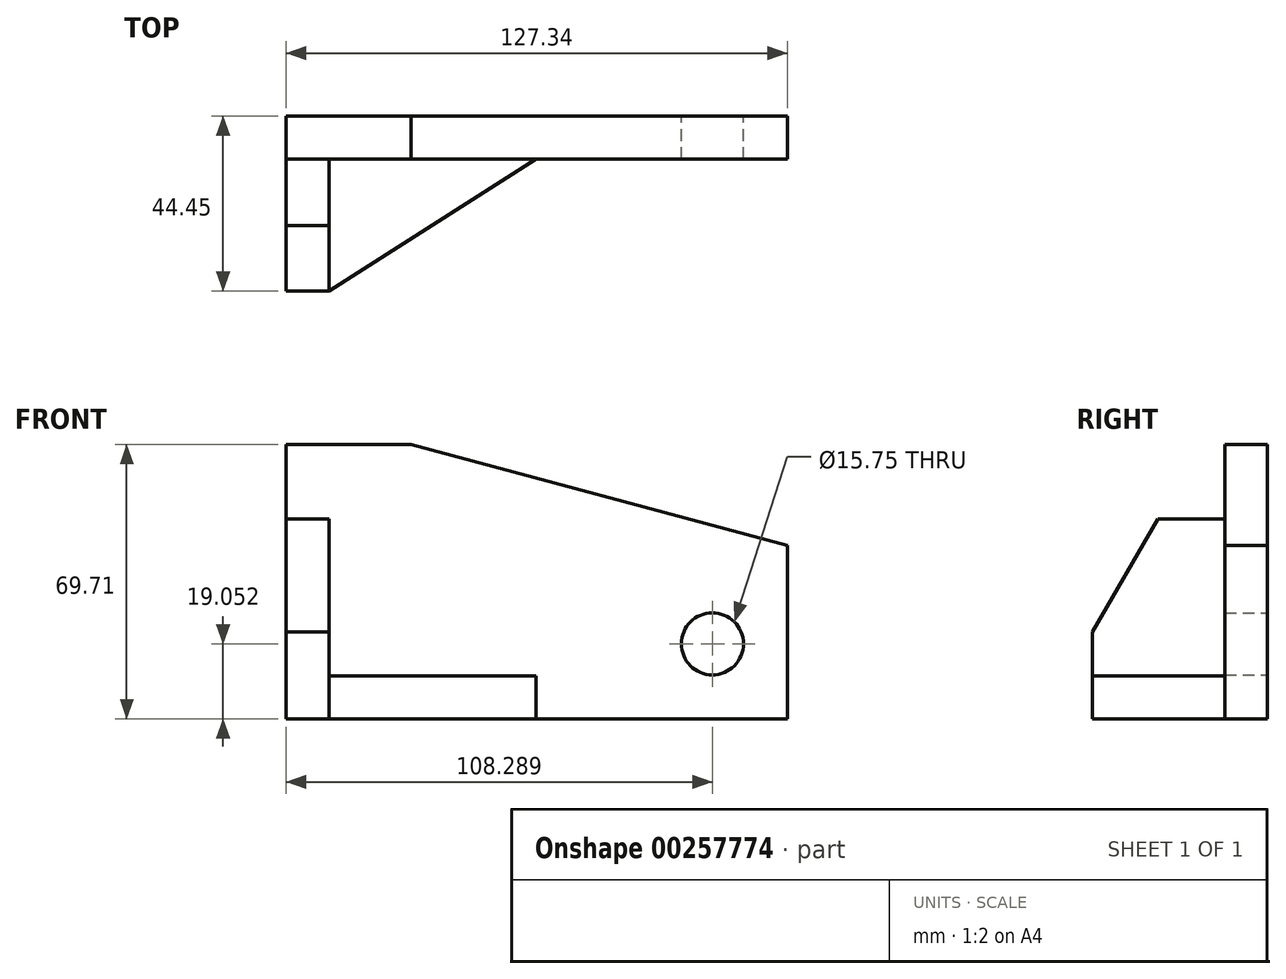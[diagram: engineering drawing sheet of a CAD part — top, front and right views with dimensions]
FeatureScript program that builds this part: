
annotation { "Feature Type Name" : "Feature", "Feature Type Description" : "" }
export const myFeature = defineFeature(function(context is Context, id is Id, definition is map)
    precondition{}
    {
        {
            var Q0;
            Q0=qCreatedBy(makeId("Front.planeOp"),FACE);
            var sketch = newSketch(context, id + "F0", { "sketchPlane" : qUnion([Q0])});
            skLineSegment(sketch, "E0.bottom", {"start": v(-78.15, 58.66) * mm, "end": v(-46.4, 58.66) * mm});
            skLineSegment(sketch, "E0.top", {"start": v(-78.15, -11.05) * mm, "end": v(49.19, -11.05) * mm});
            skLineSegment(sketch, "E0.left", {"start": v(-78.15, 58.66) * mm, "end": v(-78.15, -11.05) * mm});
            skLineSegment(sketch, "E0.right", {"start": v(49.19, 33.04) * mm, "end": v(49.19, -11.05) * mm});
            skLineSegment(sketch, "E1", {"start": v(-46.4, 58.66) * mm, "end": v(49.19, 33.04) * mm});
            skCircle(sketch, "E2", {"center": v(30.14, 8) * mm, "radius": 7.87 * mm});
            skSolve(sketch);
        }
        {
            var Q0;
            Q0=makeQuery(id+"F0.imprint","IMPRINT",FACE,{"disambiguationData":[TD([[makeQuery(id+"F0.imprint","IMPRINT",EDGE,{"derivedFrom":sQuery(id+"F0.wireOp",EDGE,"E0.bottom")}),-1.0]])]});
            extrude(context, id + "F1", {"entities" : qUnion([Q0]), "depth" : 10.92 * mm});
        }
        {
            var Q0;
            Q0=makeQuery(id+"F1.opExtrude","CAP_FACE",FACE,{"disambiguationData":[OSD([sQuery(id+"F0.wireOp",EDGE,"E0.bottom"),sQuery(id+"F0.wireOp",EDGE,"E0.top"),sQuery(id+"F0.wireOp",EDGE,"E0.left"),sQuery(id+"F0.wireOp",EDGE,"E0.right"),sQuery(id+"F0.wireOp",EDGE,"E1")])],"isStart":false});
            var sketch = newSketch(context, id + "F2", { "sketchPlane" : qUnion([Q0])});
            skLineSegment(sketch, "E3.bottom", {"start": v(-78.15, 39.75) * mm, "end": v(-67.22, 39.75) * mm});
            skLineSegment(sketch, "E3.top", {"start": v(-78.15, -11.05) * mm, "end": v(-67.22, -11.05) * mm});
            skLineSegment(sketch, "E3.left", {"start": v(-78.15, 39.75) * mm, "end": v(-78.15, -11.05) * mm});
            skLineSegment(sketch, "E3.right", {"start": v(-67.22, 39.75) * mm, "end": v(-67.22, -11.05) * mm});
            skLineSegment(sketch, "E4.bottom", {"start": v(-67.22, -11.05) * mm, "end": v(-14.65, -11.05) * mm});
            skLineSegment(sketch, "E4.top", {"start": v(-67.22, -0.13) * mm, "end": v(-14.65, -0.13) * mm});
            skLineSegment(sketch, "E4.left", {"start": v(-67.22, -11.05) * mm, "end": v(-67.22, -0.13) * mm});
            skLineSegment(sketch, "E5", {"start": v(-14.65, -0.13) * mm, "end": v(-14.65, -11.05) * mm});
            skSolve(sketch);
        }
        {
            var Q0;
            Q0=makeQuery(id+"F2.imprint","IMPRINT",FACE,{"disambiguationData":[TD([[makeQuery(id+"F2.imprint","IMPRINT",EDGE,{"derivedFrom":sQuery(id+"F2.wireOp",EDGE,"E3.bottom")}),-1.0]])]});
            var Q1;
            Q1=makeQuery(id+"F2.imprint","IMPRINT",FACE,{"disambiguationData":[TD([[makeQuery(id+"F2.imprint","IMPRINT",EDGE,{"derivedFrom":sQuery(id+"F2.wireOp",EDGE,"E4.bottom")}),1.0]])]});
            extrude(context, id + "F3", {"entities" : qUnion([Q0, Q1]), "operationType" : NewBodyOperationType.ADD, "depth" : 33.53 * mm});
        }
        {
            var Q0;
            Q0=makeQuery(id+"F3.opExtrude","CAP_EDGE",EDGE,{"disambiguationData":[OSD([sQuery(id+"F2.wireOp",EDGE,"E3.bottom")])],"isStart":false});
            chamfer(context, id + "F4", {"entities" : qUnion([Q0]), "chamferType" : ChamferType.OFFSET_ANGLE, "width" : 28.7 * mm, "oppositeDirection" : true, "angle" : 30 * degree, "tangentPropagation" : true});
        }
        {
            var Q0;
            Q0=makeQuery(id+"F3.opExtrude","SWEPT_FACE",FACE,{"disambiguationData":[OSD([sQuery(id+"F2.wireOp",EDGE,"E4.top")])]});
            var sketch = newSketch(context, id + "F5", { "sketchPlane" : qUnion([Q0])});
            skLineSegment(sketch, "E6", {"start": v(-67.22, -44.45) * mm, "end": v(-14.65, -10.92) * mm});
            skLineSegment(sketch, "E7", {"start": v(-14.65, -10.92) * mm, "end": v(-14.65, -44.45) * mm});
            skLineSegment(sketch, "E8", {"start": v(-14.65, -44.45) * mm, "end": v(-67.22, -44.45) * mm});
            skSolve(sketch);
        }
        {
            var Q0;
            Q0=makeQuery(id+"F5.imprint","IMPRINT",FACE,{"disambiguationData":[TD([[makeQuery(id+"F5.imprint","IMPRINT",EDGE,{"derivedFrom":sQuery(id+"F5.wireOp",EDGE,"E6")}),-1.0]])]});
            extrude(context, id + "F6", {"entities" : qUnion([Q0]), "operationType" : NewBodyOperationType.REMOVE, "endBound" : BoundingType.THROUGH_ALL, "oppositeDirection" : true, "depth" : 25.4 * mm});
        }
    });
